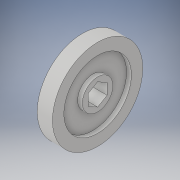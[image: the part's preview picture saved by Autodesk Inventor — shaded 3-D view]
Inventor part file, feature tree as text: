
AUTODESK INVENTOR PART (.ipt)
format: ipt  version: 2018 (Build 220112000, 112)  size: 134,656 bytes
history: native  units: in
note: dims shown in document units (in); Inventor stores cm internally (conversion verified against a paired STEP export)
features: extrude x3, sketch x3
ambient origin geometry x8: Origin, YZ Plane, XZ Plane, XY Plane, X Axis, Y Axis, Z Axis, Center Point
bodies: Solid1 (feature_tree)
feature tree (6):
  extrude  "Extrusion1"  Depth=0.8in
  extrude  "Extrusion2"  Depth=0.4in TaperAngle=0.0deg
  extrude  "Extrusion3"  Depth=0.125in
  sketch  "Sketch1"  dims[d0=2.375in d1=0.8in]
  sketch  "Sketch2"  dims[d2=0.5in d3=0.4in d4=0.0in]
  sketch  "Sketch3"  dims[d5=1.775in d6=0.8in d7=0.125in d8=0.0in d9=0.8in d10=1.775in d11=0.125in d12=0.0in]
